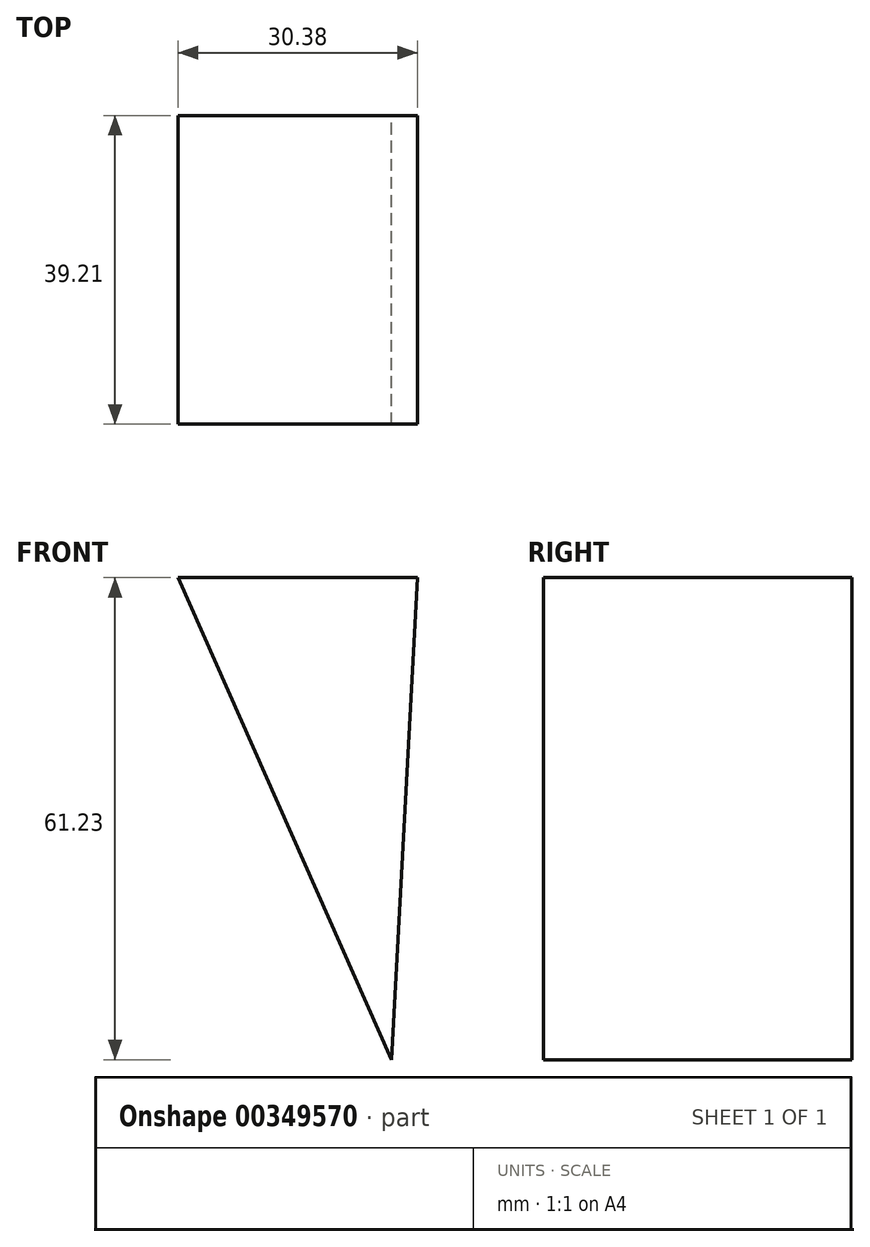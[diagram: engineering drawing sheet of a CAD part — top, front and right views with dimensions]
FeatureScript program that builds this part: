
annotation { "Feature Type Name" : "Feature", "Feature Type Description" : "" }
export const myFeature = defineFeature(function(context is Context, id is Id, definition is map)
    precondition{}
    {
        {
            var Q0;
            Q0=qCreatedBy(makeId("Front.planeOp"),FACE);
            var sketch = newSketch(context, id + "F0", { "sketchPlane" : qUnion([Q0])});
            skLineSegment(sketch, "E0", {"start": v(-47.75, 132.62) * mm, "end": v(-17.37, 132.62) * mm});
            skLineSegment(sketch, "E1", {"start": v(-17.37, 132.62) * mm, "end": v(-20.68, 71.39) * mm});
            skLineSegment(sketch, "E2", {"start": v(-20.68, 71.39) * mm, "end": v(-47.75, 132.62) * mm});
            skSolve(sketch);
        }
        {
            var Q0;
            Q0 = qSketchRegion(id + "F0", true);
            extrude(context, id + "F1", {"entities" : qUnion([Q0]), "depth" : 39.2 * mm});
        }
    });
